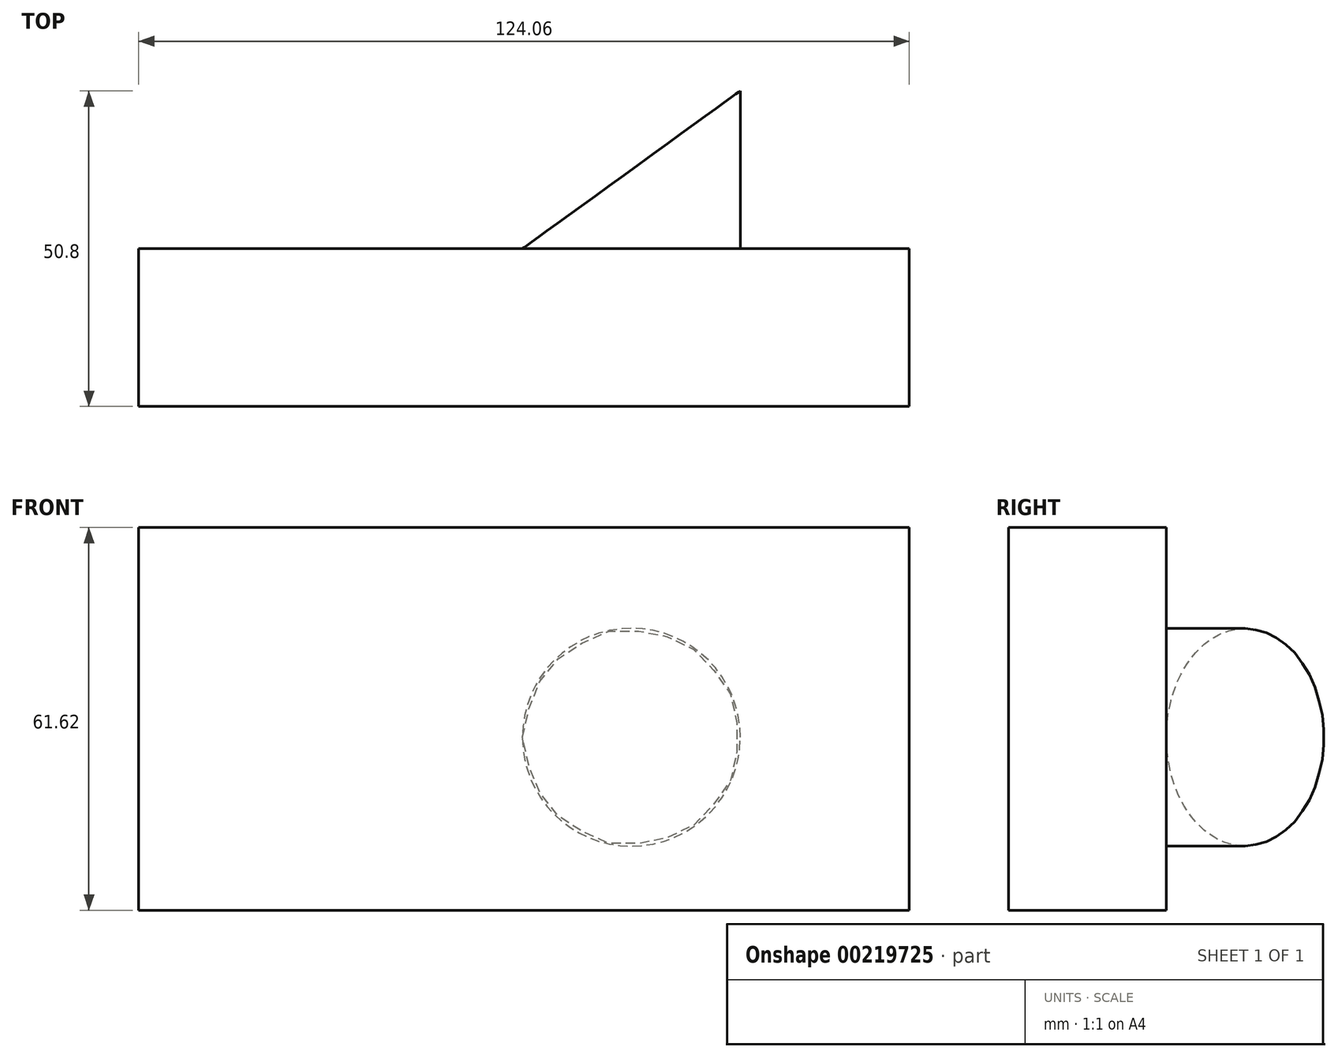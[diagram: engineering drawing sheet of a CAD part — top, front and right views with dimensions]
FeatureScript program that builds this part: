
annotation { "Feature Type Name" : "Feature", "Feature Type Description" : "" }
export const myFeature = defineFeature(function(context is Context, id is Id, definition is map)
    precondition{}
    {
        {
            var Q0;
            Q0=qCreatedBy(makeId("Front.planeOp"),FACE);
            var sketch = newSketch(context, id + "F0", { "sketchPlane" : qUnion([Q0])});
            skLineSegment(sketch, "E0.bottom", {"start": v(-62.03, 30.8) * mm, "end": v(62.03, 30.8) * mm});
            skLineSegment(sketch, "E0.top", {"start": v(-62.03, -30.8) * mm, "end": v(62.03, -30.8) * mm});
            skLineSegment(sketch, "E0.left", {"start": v(-62.03, 30.8) * mm, "end": v(-62.03, -30.8) * mm});
            skLineSegment(sketch, "E0.right", {"start": v(62.03, 30.8) * mm, "end": v(62.03, -30.8) * mm});
            skPoint(sketch, "E0.middle", {"position": v(0, 0) * mm});
            skSolve(sketch);
        }
        {
            var Q0;
            Q0=makeQuery(id+"F0.imprint","IMPRINT",FACE,{"disambiguationData":[TD([[makeQuery(id+"F0.imprint","IMPRINT",EDGE,{"derivedFrom":sQuery(id+"F0.wireOp",EDGE,"E0.bottom")}),-1.0]])]});
            extrude(context, id + "F1", {"entities" : qUnion([Q0]), "depth" : 25.4 * mm});
        }
        {
            var Q0;
            Q0=makeQuery(id+"F1.opExtrude","CAP_FACE",FACE,{"disambiguationData":[OSD([sQuery(id+"F0.wireOp",EDGE,"E0.bottom"),sQuery(id+"F0.wireOp",EDGE,"E0.top"),sQuery(id+"F0.wireOp",EDGE,"E0.left"),sQuery(id+"F0.wireOp",EDGE,"E0.right")])],"isStart":true});
            var sketch = newSketch(context, id + "F2", { "sketchPlane" : qUnion([Q0])});
            skCircle(sketch, "E1", {"center": v(-17.29, -2.96) * mm, "radius": 17.54 * mm});
            skPoint(sketch, "E1.first.point", {"position": v(0, 0) * mm});
            skPoint(sketch, "E1.second.point", {"position": v(-34.58, 0) * mm});
            skPoint(sketch, "E1.third.point", {"position": v(-31.76, -12.87) * mm});
            skSolve(sketch);
        }
        {
            var Q0;
            Q0=makeQuery(id+"F2.imprint","IMPRINT",FACE,{"disambiguationData":[TD([[makeQuery(id+"F2.imprint","IMPRINT",EDGE,{"derivedFrom":sQuery(id+"F2.wireOp",EDGE,"E1")}),1.0]])]});
            extrude(context, id + "F3", {"entities" : qUnion([Q0]), "operationType" : NewBodyOperationType.ADD, "depth" : 25.4 * mm});
        }
        {
            var Q0;
            Q0=makeQuery(id+"F1.opExtrude","SWEPT_FACE",FACE,{"disambiguationData":[OSD([sQuery(id+"F0.wireOp",EDGE,"E0.top")])]});
            var sketch = newSketch(context, id + "F4", { "sketchPlane" : qUnion([Q0])});
            skLineSegment(sketch, "E2.0", {"start": v(34.83, -25.4) * mm, "end": v(-0.25, -25.4) * mm});
            skLineSegment(sketch, "E3", {"start": v(-0.25, -25.4) * mm, "end": v(-0.25, 0) * mm});
            skLineSegment(sketch, "E4", {"start": v(-0.25, 0) * mm, "end": v(34.83, -25.4) * mm});
            skSolve(sketch);
        }
        {
            var Q0;
            Q0 = qSketchRegion(id + "F4", true);
            extrude(context, id + "F5", {"entities" : qUnion([Q0]), "operationType" : NewBodyOperationType.REMOVE, "endBound" : BoundingType.THROUGH_ALL, "oppositeDirection" : true, "depth" : 25.4 * mm});
        }
    });
